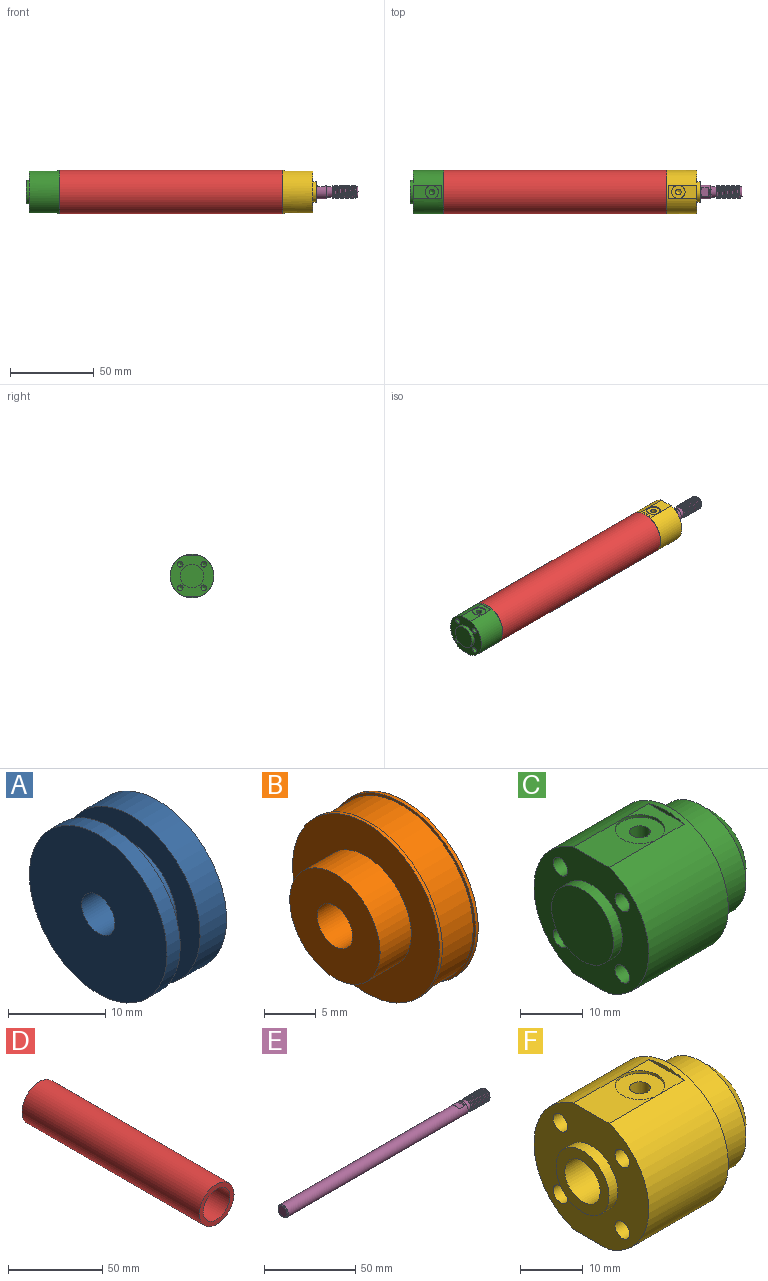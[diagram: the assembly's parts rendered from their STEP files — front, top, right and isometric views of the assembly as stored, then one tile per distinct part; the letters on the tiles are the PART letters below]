
ASSEMBLY  parts=6 mates=5
PART A: 10 faces, bbox 8.7x20x20 mm
  f0: cylinder r=2.4mm len=4.8mm, axis (-1,0,0), area 72.4mm2, adj f1,f9
  f1: plane 12.3x12.3mm, normal (1,0,0), area 100.7mm2, adj f0,f2
  f2: cylinder r=6.15mm len=12.3mm, axis (-1,0,0), area 148.8mm2, adj f1,f3
  f3: plane 20x20mm, normal (1,0,0), area 195.3mm2, adj f2,f4
  f4: cylinder r=10mm len=20mm, axis (-1,0,0), area 241.9mm2, adj f3,f5
  f5: plane 20x20mm, normal (-1,0,0), area 175.6mm2, adj f4,f6
  f6: cylinder r=6.64mm len=13.28mm, axis (-1,0,0), area 120.2mm2, adj f5,f7
  f7: plane 20x20mm, normal (1,0,0), area 175.6mm2, adj f6,f8
  f8: cylinder r=10mm len=20mm, axis (-1,0,0), area 120.6mm2, adj f7,f9
  f9: plane 20x20mm, normal (-1,0,0), area 296.1mm2, adj f0,f8
PART B: 12 faces, bbox 9.5x20x20 mm
  f0: cylinder r=9.7mm len=19.4mm, axis (-1,0,0), area 274.3mm2, adj f1,f11
  f1: plane 20x20mm, normal (1,0,0), area 18.6mm2, adj f0,f2
  f2: cylinder r=10mm len=20mm, axis (-1,0,0), area 24.5mm2, adj f1,f3
  f3: plane 20x20mm, normal (-1,0,0), area 195.3mm2, adj f2,f4
  f4: cylinder r=6.15mm len=12.3mm, axis (-1,0,0), area 163.6mm2, adj f3,f5
  f5: plane 12.3x12.3mm, normal (-1,0,0), area 100.7mm2, adj f4,f6
  f6: cylinder r=2.4mm len=5.19mm, axis (-1,0,0), area 78.3mm2, adj f5,f7
  f7: plane 10x10mm, normal (1,0,0), area 60.4mm2, adj f6,f8
  f8: cylinder r=5mm len=10mm, axis (-1,0,0), area 135.7mm2, adj f7,f9
  f9: plane 20x20mm, normal (1,0,0), area 235.6mm2, adj f8,f10
  f10: cylinder r=10mm len=20mm, axis (-1,0,0), area 24.5mm2, adj f9,f11
  f11: plane 20x20mm, normal (-1,0,0), area 18.6mm2, adj f0,f10
PART C: 31 faces, bbox 29.5x26x26 mm
  f0: cylinder r=10mm len=20mm, axis (-1,0,0), area 439.8mm2, adj f4,f30
  f1: plane 11x8mm, normal (0,0,1), area 62.9mm2, adj f2,f3,f19
  f2: cylinder r=13mm len=26mm, axis (1,0,0), area 1193.7mm2, adj f1,f3,f4,f15,f16,f17,f18,f23
  f3: plane 26x24.74mm, normal (-1,0,0), area 336mm2, adj f1,f2,f5,f7,f9,f11,f13,f15
  f4: plane 26x26mm, normal (1,0,0), area 216.8mm2, adj f0,f2
  f5: cylinder r=7mm len=14mm, axis (1,0,0), area 88mm2, adj f3,f6
  f6: plane 14x14mm, normal (-1,0,0), area 153.9mm2, adj f5
  f7: cylinder r=1.65mm len=7mm, axis (-1,0,0), area 72.6mm2, adj f3,f8
  f8: cone r=0mm half-angle=59deg, axis (-1,0,0), area 10mm2, adj f7
  f9: cylinder r=1.65mm len=7mm, axis (-1,0,0), area 72.6mm2, adj f3,f10
  f10: cone r=0mm half-angle=59deg, axis (-1,0,0), area 10mm2, adj f9
  f11: cylinder r=1.65mm len=7mm, axis (-1,0,0), area 72.6mm2, adj f3,f12
  f12: cone r=0mm half-angle=59deg, axis (-1,0,0), area 10mm2, adj f11
  f13: cylinder r=1.65mm len=7mm, axis (-1,0,0), area 72.6mm2, adj f3,f14
  f14: cone r=0mm half-angle=59deg, axis (-1,0,0), area 10mm2, adj f13
  f15: plane 17x8mm, normal (0,0,-1), area 85.8mm2, adj f2,f3,f16,f23
  f16: plane 8x0.63mm, normal (-1,0,0), area 3.4mm2, adj f2,f15
  f17: plane 8x6mm, normal (0,0,1), area 22.9mm2, adj f2,f18,f19
  f18: plane 8x0.63mm, normal (-1,0,0), area 3.4mm2, adj f2,f17
  f19: cylinder r=4mm len=8mm, axis (0,0,1), area 12.6mm2, adj f1,f17,f20
  f20: plane 8x8mm, normal (0,0,1), area 41.7mm2, adj f19,f22
  f21: cone r=0mm half-angle=59deg, axis (0,0,1), area 10mm2, adj f22
  f22: cylinder r=1.65mm len=4.7mm, axis (0,0,1), area 48.7mm2, adj f20,f21
  f23: cylinder r=4mm len=8mm, axis (0,0,-1), area 12.6mm2, adj f2,f15,f24
  f24: plane 8x8mm, normal (0,0,-1), area 41.7mm2, adj f23,f26
  f25: cone r=0mm half-angle=59deg, axis (0,0,-1), area 10mm2, adj f26
  f26: cylinder r=1.65mm len=4.7mm, axis (0,0,-1), area 48.7mm2, adj f24,f25
  f27: plane 15x15mm, normal (1,0,0), area 98.2mm2, adj f29,f30
  f28: plane 10x10mm, normal (1,0,0), area 78.5mm2, adj f29
  f29: cylinder r=5mm len=10mm, axis (1,0,0), area 298.5mm2, adj f27,f28
  f30: cone r=7.5mm half-angle=45deg, axis (-1,0,0), area 194.4mm2, adj f0,f27
PART D: 4 faces, bbox 26x133x26 mm
  f0: cylinder r=10mm len=133mm, axis (0,1,0), area 8356.6mm2, adj f2,f3
  f1: cylinder r=13mm len=133mm, axis (0,1,0), area 10863.6mm2, adj f2,f3
  f2: plane 26x26mm, normal (0,-1,0), area 216.8mm2, adj f0,f1
  f3: plane 26x26mm, normal (0,1,0), area 216.8mm2, adj f0,f1
PART E: 19 faces, bbox 158.4x8x9.2 mm
  f0: plane 7x7mm, normal (-1,0,0), area 5.3mm2, adj f4,f16
  f1: cylinder r=4mm len=139.43mm, axis (1,0,0), area 3476.7mm2, adj f7,f8,f9,f14,f15,f17,f18
  f2: plane 5x5mm, normal (1,0,0), area 19.6mm2, adj f13
  f3: cylinder r=4mm len=13.5mm, axis (1,0,0), area 2.5mm2, adj f10,f11,f12,f13,f16
  f4: cylinder r=3.25mm len=6.5mm, axis (1,0,0), area 51.1mm2, adj f0,f5
  f5: plane 7x7mm, normal (1,0,0), area 5.3mm2, adj f4,f17
  f6: plane 7x7mm, normal (-1,0,0), area 38.5mm2, adj f18
  f7: plane 5.29x0mm, normal (1,0,0), area 0mm2, adj f1,f9,f15
  f8: plane 5.29x0mm, normal (-1,0,0), area 0mm2, adj f1,f9,f14
  f9: plane 5.29x4mm, normal (0,0,1), area 21.2mm2, adj f1,f7,f8
  f10: bspline ~15.12x9.24mm, area 281.9mm2, adj f3,f11,f12,f13
  f11: plane 0.78x0.63mm, normal (0,0,-1), area 0.2mm2, adj f3,f10,f12,f16
  f12: bspline ~15.12x9.24mm, area 289.3mm2, adj f3,f10,f11,f13,f16
  f13: cone r=2.5mm half-angle=45deg, axis (-1,0,0), area 31.7mm2, adj f2,f3,f10,f12
  f14: plane 5.28x1mm, normal (-0.87,0,0.5), area 4.2mm2, adj f1,f8
  f15: plane 5.28x1mm, normal (0.87,0,0.5), area 4.2mm2, adj f1,f7
  f16: cone r=4mm half-angle=45deg, axis (1,0,0), area 10.6mm2, adj f0,f3,f11,f12
  f17: cone r=3.5mm half-angle=45deg, axis (-1,0,0), area 16.7mm2, adj f1,f5
  f18: cone r=4mm half-angle=45deg, axis (1,0,0), area 16.7mm2, adj f1,f6
PART F: 32 faces, bbox 29.5x26x26 mm
  f0: plane 11x8mm, normal (0,0,1), area 62.9mm2, adj f1,f2,f24
  f1: cylinder r=13mm len=26mm, axis (1,0,0), area 1193.7mm2, adj f0,f2,f5,f20,f21,f22,f23,f28
  f2: plane 26x24.74mm, normal (-1,0,0), area 376.9mm2, adj f0,f1,f6,f8,f10,f12,f14,f20
  f3: plane 10x10mm, normal (1,0,0), area 28.3mm2, adj f4,f16
  f4: cylinder r=4mm len=20mm, axis (1,0,0), area 502.7mm2, adj f3,f7
  f5: plane 26x26mm, normal (1,0,0), area 216.8mm2, adj f1,f17
  f6: cylinder r=6mm len=12mm, axis (1,0,0), area 75.4mm2, adj f2,f7
  f7: plane 12x12mm, normal (-1,0,0), area 62.8mm2, adj f4,f6
  f8: cylinder r=1.65mm len=7mm, axis (-1,0,0), area 72.6mm2, adj f2,f9
  f9: cone r=0mm half-angle=59deg, axis (-1,0,0), area 10mm2, adj f8
  f10: cylinder r=1.65mm len=7mm, axis (-1,0,0), area 72.6mm2, adj f2,f11
  f11: cone r=0mm half-angle=59deg, axis (-1,0,0), area 10mm2, adj f10
  f12: cylinder r=1.65mm len=7mm, axis (-1,0,0), area 72.6mm2, adj f2,f13
  f13: cone r=0mm half-angle=59deg, axis (-1,0,0), area 10mm2, adj f12
  f14: cylinder r=1.65mm len=7mm, axis (-1,0,0), area 72.6mm2, adj f2,f15
  f15: cone r=0mm half-angle=59deg, axis (-1,0,0), area 10mm2, adj f14
  f16: cylinder r=5mm len=10mm, axis (-1,0,0), area 298.5mm2, adj f3,f18
  f17: cylinder r=10mm len=20mm, axis (-1,0,0), area 439.8mm2, adj f5,f19
  f18: plane 15x15mm, normal (1,0,0), area 98.2mm2, adj f16,f19
  f19: cone r=7.5mm half-angle=45deg, axis (-1,0,0), area 194.4mm2, adj f17,f18
  f20: plane 17x8mm, normal (0,0,-1), area 85.8mm2, adj f1,f2,f21,f28
  f21: plane 8x0.63mm, normal (-1,0,0), area 3.4mm2, adj f1,f20
  f22: plane 8x6mm, normal (0,0,1), area 22.9mm2, adj f1,f23,f24
  f23: plane 8x0.63mm, normal (-1,0,0), area 3.4mm2, adj f1,f22
  f24: cylinder r=4mm len=8mm, axis (0,0,1), area 12.6mm2, adj f0,f22,f25
  f25: plane 8x8mm, normal (0,0,1), area 41.7mm2, adj f24,f27
  f26: cone r=0mm half-angle=59deg, axis (0,0,1), area 10mm2, adj f27
  f27: cylinder r=1.65mm len=4.7mm, axis (0,0,1), area 48.7mm2, adj f25,f26
  f28: cylinder r=4mm len=8mm, axis (0,0,-1), area 12.6mm2, adj f1,f20,f29
  f29: plane 8x8mm, normal (0,0,-1), area 41.7mm2, adj f28,f31
  f30: cone r=0mm half-angle=59deg, axis (0,0,-1), area 10mm2, adj f31
  f31: cylinder r=1.65mm len=4.7mm, axis (0,0,-1), area 48.7mm2, adj f29,f30
PLACE A t=(-427.02,-75.07,25.98)mm
PLACE B t=(-427.22,-75.07,25.98)mm
PLACE C rot(axis=(-1,0,0),180deg) t=(-441.52,-75.07,25.98)mm
PLACE D rot(axis=(-0.71,0.71,0),180deg) t=(-441.52,-75.07,25.98)mm
PLACE E t=(-422.03,-75.07,25.98)mm
PLACE F rot(axis=(0,0,-1),180deg) t=(-308.52,-75.07,25.98)mm
MATE fastened F.f16 <-> D.f0  axis (1,0,0) through (-308.52,-75.07,25.98)mm
MATE fastened D.f0 <-> C.f30  axis (-1,0,0) through (-441.52,-75.07,25.98)mm
MATE fastened B.f0 <-> A.f0  axis (-1,0,0) through (-427.22,-75.07,25.98)mm
MATE slider D.f0 <-> A.f0  axis (-1,0,0) through (-441.52,-75.07,25.98)mm
MATE fastened B.f0 <-> E.f1  axis (1,0,0) through (-422.03,-75.07,25.98)mm
